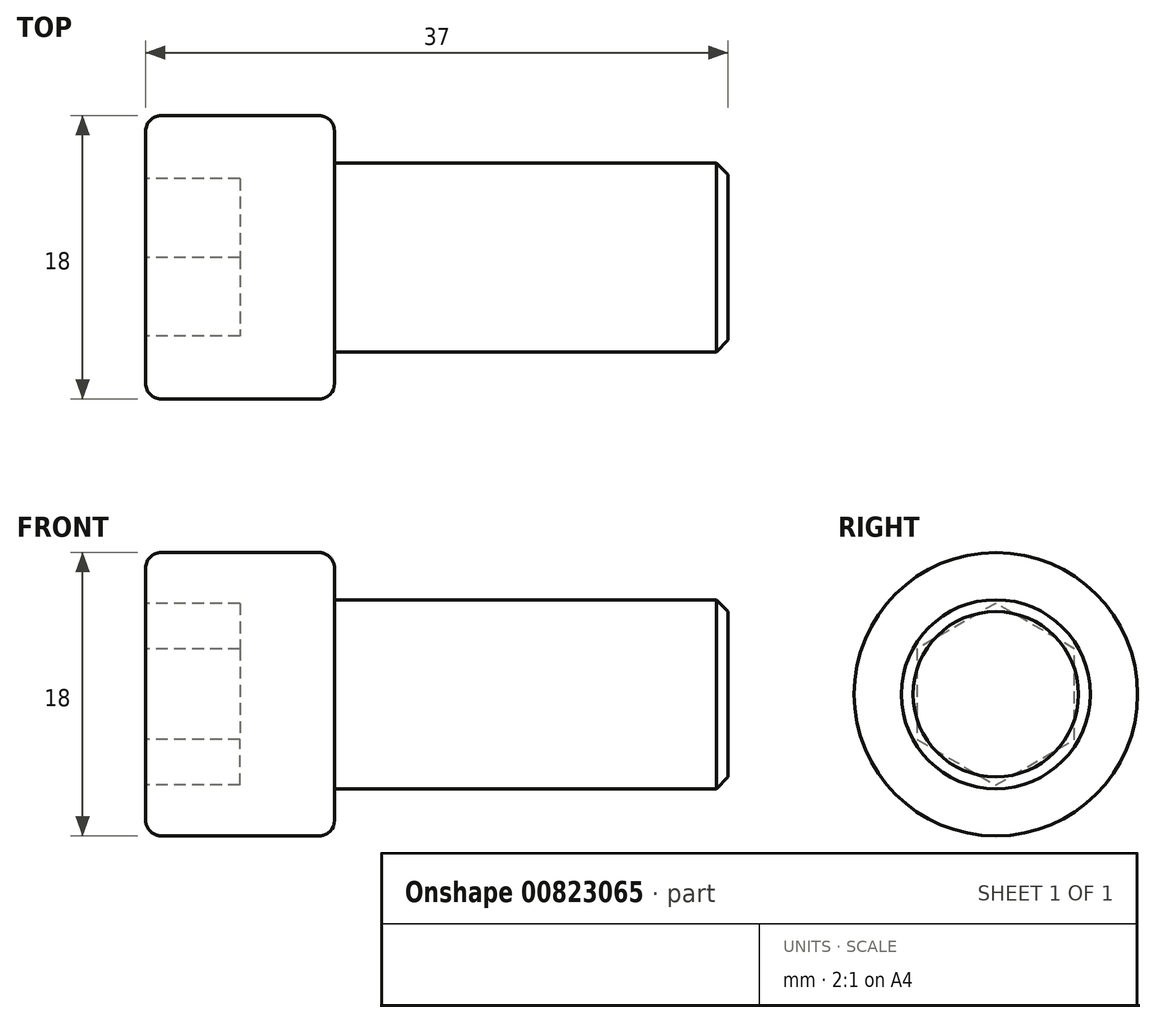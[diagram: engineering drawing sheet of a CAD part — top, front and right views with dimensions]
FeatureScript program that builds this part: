
annotation { "Feature Type Name" : "Feature", "Feature Type Description" : "" }
export const myFeature = defineFeature(function(context is Context, id is Id, definition is map)
    precondition{}
    {
        {
            var Q0;
            Q0=qCreatedBy(makeId("Front.planeOp"),FACE);
            var sketch = newSketch(context, id + "F0", { "sketchPlane" : qUnion([Q0])});
            skLineSegment(sketch, "E0", {"start": v(0, 0) * mm, "end": v(0, 6) * mm});
            skLineSegment(sketch, "E1", {"start": v(0, 6) * mm, "end": v(-25, 6) * mm});
            skLineSegment(sketch, "E2", {"start": v(-25, 6) * mm, "end": v(-25, 9) * mm});
            skLineSegment(sketch, "E3", {"start": v(-25, 9) * mm, "end": v(-37, 9) * mm});
            skLineSegment(sketch, "E4", {"start": v(-37, 9) * mm, "end": v(-37, 0) * mm});
            skLineSegment(sketch, "E5", {"start": v(-37, 0) * mm, "end": v(0, 0) * mm});
            skLineSegment(sketch, "E6", {"start": v(0, 0) * mm, "end": v(7.25, 0) * mm, "construction": true});
            skSolve(sketch);
        }
        {
            var Q0;
            Q0=makeQuery(id+"F0.imprint","IMPRINT",FACE,{"disambiguationData":[TD([[makeQuery(id+"F0.imprint","IMPRINT",EDGE,{"derivedFrom":sQuery(id+"F0.wireOp",EDGE,"E0")}),1.0]])]});
            var Q1;
            Q1=sQuery(id+"F0.wireOp",EDGE,"E6");
            revolve(context, id + "F1", {"surfaceOperationType" : NewSurfaceOperationType.NEW, "entities" : qUnion([Q0]), "axis" : qUnion([Q1]), "revolveType" : RevolveType.FULL});
        }
        {
            var Q0;
            Q0=makeQuery(id+"F1.opRevolve","SWEPT_EDGE",EDGE,{"disambiguationData":[OSD([sQuery(id+"F0.wireOp",EDGE,"E0"),sQuery(id+"F0.wireOp",EDGE,"E1")])]});
            chamfer(context, id + "F2", {"entities" : qUnion([Q0]), "width" : 0.75 * mm, "tangentPropagation" : true});
        }
        {
            var Q0;
            Q0=makeQuery(id+"F1.opRevolve","SWEPT_FACE",FACE,{"disambiguationData":[OSD([sQuery(id+"F0.wireOp",EDGE,"E3")])]});
            fillet(context, id + "F3", {"entities" : qUnion([Q0]), "radius" : 1 * mm, "tangentPropagation" : true, "allowEdgeOverflow" : false});
        }
        {
            var Q0;
            Q0=makeQuery(id+"F1.opRevolve","SWEPT_FACE",FACE,{"disambiguationData":[OSD([sQuery(id+"F0.wireOp",EDGE,"E4")])]});
            var sketch = newSketch(context, id + "F4", { "sketchPlane" : qUnion([Q0])});
            skLineSegment(sketch, "E7", {"start": v(0, 0) * mm, "end": v(8.98, 0) * mm, "construction": true});
            skCircle(sketch, "E8.cCircle", {"center": v(0, 0) * mm, "radius": 5 * mm, "construction": true});
            skLineSegment(sketch, "E8.0", {"start": v(5, 2.89) * mm, "end": v(5, -2.89) * mm});
            skLineSegment(sketch, "E8.1", {"start": v(5, -2.89) * mm, "end": v(0, -5.77) * mm});
            skLineSegment(sketch, "E8.2", {"start": v(0, -5.77) * mm, "end": v(-5, -2.89) * mm});
            skLineSegment(sketch, "E8.3", {"start": v(-5, -2.89) * mm, "end": v(-5, 2.89) * mm});
            skLineSegment(sketch, "E8.4", {"start": v(-5, 2.89) * mm, "end": v(0, 5.77) * mm});
            skLineSegment(sketch, "E8.5", {"start": v(0, 5.77) * mm, "end": v(5, 2.89) * mm});
            skPoint(sketch, "E8.0.midPoint", {"position": v(5, 0) * mm});
            skSolve(sketch);
        }
        {
            var Q0;
            Q0=qSketchRegion(id+"F4",true);
            extrude(context, id + "F5", {"entities" : qUnion([Q0]), "operationType" : NewBodyOperationType.REMOVE, "oppositeDirection" : true, "depth" : 6 * mm, "offsetDistance" : 25 * mm});
        }
    });
